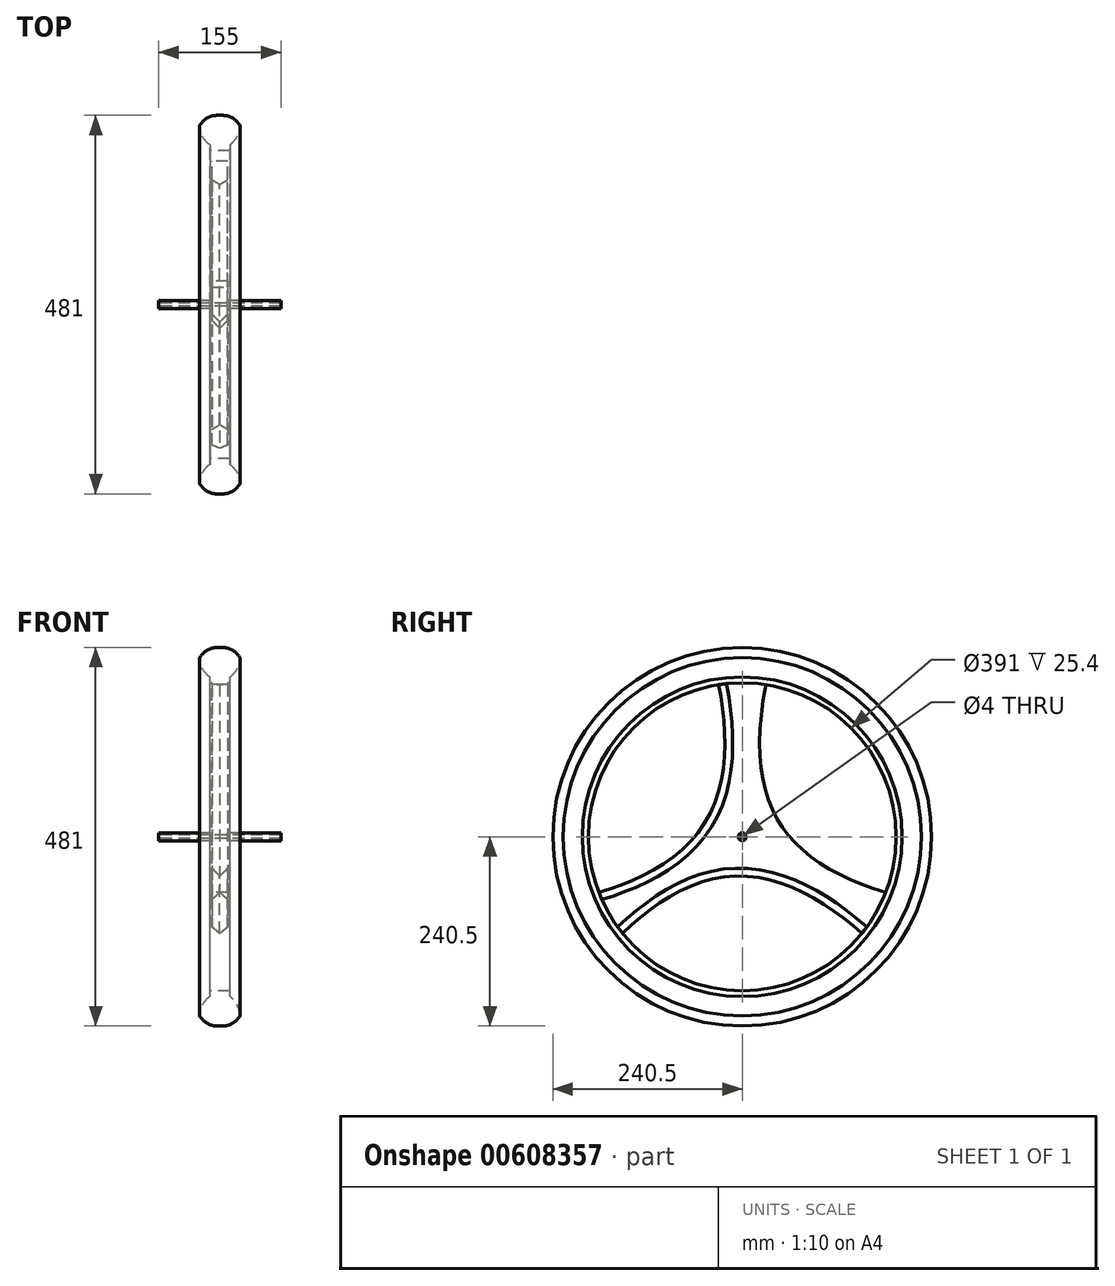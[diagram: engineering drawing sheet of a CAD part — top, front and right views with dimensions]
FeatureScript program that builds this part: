
annotation { "Feature Type Name" : "Feature", "Feature Type Description" : "" }
export const myFeature = defineFeature(function(context is Context, id is Id, definition is map)
    precondition{}
    {
        {
            var Q0;
            Q0=qCreatedBy(makeId("Right.planeOp"),FACE);
            var sketch = newSketch(context, id + "F0", { "sketchPlane" : qUnion([Q0])});
            skCircle(sketch, "E0", {"center": v(0, 0) * mm, "radius": 195.5 * mm});
            skCircle(sketch, "E1.0", {"center": v(0, 0) * mm, "radius": 240.5 * mm});
            skCircle(sketch, "E2", {"center": v(0, 0) * mm, "radius": 5 * mm});
            skCircle(sketch, "E3", {"center": v(0, 0) * mm, "radius": 2 * mm});
            skLineSegment(sketch, "E4", {"start": v(0, 0) * mm, "end": v(0, 195.5) * mm, "construction": true});
            skLineSegment(sketch, "E5", {"start": v(0, 0) * mm, "end": v(-169.3, -97.75) * mm, "construction": true});
            skLineSegment(sketch, "E6", {"start": v(0, 0) * mm, "end": v(169.3, -97.75) * mm, "construction": true});
            skFitSpline(sketch, "E7", {"points": [v(30, 193.18) * mm, v(182.3, -70.61) * mm], "startDerivative": vector(-90, -465.62) * mm, "endDerivative": vector(378.03, -114.33) * mm});
            skFitSpline(sketch, "E8.MirrorCS", {"points": [v(-30, 193.18) * mm, v(-182.3, -70.61) * mm], "startDerivative": vector(90, -465.62) * mm, "endDerivative": vector(-378.03, -114.33) * mm});
            skFitSpline(sketch, "E9.MirrorCS", {"points": [v(30, 193.18) * mm, v(182.3, -70.61) * mm], "startDerivative": vector(-90, -465.62) * mm, "endDerivative": vector(378.03, -114.33) * mm});
            skFitSpline(sketch, "E10.MirrorCS", {"points": [v(152.3, -122.57) * mm, v(-152.3, -122.57) * mm], "startDerivative": vector(-358.24, 310.75) * mm, "endDerivative": vector(-288.03, -270.22) * mm});
            skCircle(sketch, "E11", {"center": v(0, 0) * mm, "radius": 203 * mm});
            skSolve(sketch);
        }
        {
            var Q0;
            Q0=makeQuery(id+"F0.imprint","IMPRINT",FACE,{"disambiguationData":[TD([[makeQuery(id+"F0.imprint","IMPRINT",EDGE,{"derivedFrom":sQuery(id+"F0.wireOp",EDGE,"E11")}),1.0]])]});
            extrude(context, id + "F1", {"entities" : qUnion([Q0]), "endBound" : BoundingType.SYMMETRIC, "depth" : 25.4 * mm, "offsetDistance" : 25 * mm});
        }
        {
            var Q0;
            Q0=makeQuery(id+"F0.imprint","IMPRINT",FACE,{"disambiguationData":[TD([[makeQuery(id+"F0.imprint","IMPRINT",EDGE,{"derivedFrom":sQuery(id+"F0.wireOp",EDGE,"E2")}),-1.0]])]});
            extrude(context, id + "F2", {"entities" : qUnion([Q0]), "operationType" : NewBodyOperationType.ADD, "endBound" : BoundingType.SYMMETRIC, "depth" : 20 * mm, "offsetDistance" : 25 * mm});
        }
        {
            var Q0;
            Q0=makeQuery(id+"F0.imprint","IMPRINT",FACE,{"disambiguationData":[TD([[makeQuery(id+"F0.imprint","IMPRINT",EDGE,{"derivedFrom":sQuery(id+"F0.wireOp",EDGE,"E2")}),1.0]])]});
            extrude(context, id + "F3", {"entities" : qUnion([Q0]), "operationType" : NewBodyOperationType.ADD, "endBound" : BoundingType.SYMMETRIC, "depth" : 155 * mm, "offsetDistance" : 25 * mm});
        }
        {
            var Q0;
            Q0=makeQuery(id+"F0.imprint","IMPRINT",FACE,{"disambiguationData":[TD([[makeQuery(id+"F0.imprint","IMPRINT",EDGE,{"derivedFrom":sQuery(id+"F0.wireOp",EDGE,"E1.0")}),1.0]])]});
            extrude(context, id + "F4", {"entities" : qUnion([Q0]), "operationType" : NewBodyOperationType.ADD, "endBound" : BoundingType.SYMMETRIC, "depth" : 50.8 * mm, "offsetDistance" : 25 * mm});
        }
        {
            var Q0;
            Q0=makeQuery(id+"F4.opExtrude","CAP_EDGE",EDGE,{"disambiguationData":[OSD([sQuery(id+"F0.wireOp",EDGE,"E11")])],"isStart":true});
            var Q1;
            Q1=makeQuery(id+"F4.opExtrude","CAP_EDGE",EDGE,{"disambiguationData":[OSD([sQuery(id+"F0.wireOp",EDGE,"E11")])],"isStart":false});
            fillet(context, id + "F5", {"entities" : qUnion([Q0, Q1]), "radius" : 30 * mm, "tangentPropagation" : true, "allowEdgeOverflow" : false});
        }
        {
            var Q0;
            Q0=makeQuery(id+"F4.opExtrude","CAP_EDGE",EDGE,{"disambiguationData":[OSD([sQuery(id+"F0.wireOp",EDGE,"E1.0")])],"isStart":false});
            var Q1;
            Q1=makeQuery(id+"F4.opExtrude","CAP_EDGE",EDGE,{"disambiguationData":[OSD([sQuery(id+"F0.wireOp",EDGE,"E1.0")])],"isStart":true});
            fillet(context, id + "F6", {"entities" : qUnion([Q0, Q1]), "radius" : 25.4 * mm, "tangentPropagation" : true, "allowEdgeOverflow" : false});
        }
        {
            var Q0;
            Q0=makeQuery(id+"F2.opExtrude","CAP_EDGE",EDGE,{"disambiguationData":[OSD([sQuery(id+"F0.wireOp",EDGE,"E8.MirrorCS")])],"isStart":false});
            var Q1;
            Q1=makeQuery(id+"F2.opExtrude","CAP_EDGE",EDGE,{"disambiguationData":[OSD([sQuery(id+"F0.wireOp",EDGE,"E8.MirrorCS")])],"isStart":true});
            var Q2;
            Q2=makeQuery(id+"F2.opExtrude","CAP_EDGE",EDGE,{"disambiguationData":[OSD([sQuery(id+"F0.wireOp",EDGE,"E10.MirrorCS")])],"isStart":false});
            var Q3;
            Q3=makeQuery(id+"F2.opExtrude","CAP_EDGE",EDGE,{"disambiguationData":[OSD([sQuery(id+"F0.wireOp",EDGE,"E10.MirrorCS")])],"isStart":true});
            var Q4;
            Q4=makeQuery(id+"F2.opExtrude","CAP_EDGE",EDGE,{"disambiguationData":[OSD([sQuery(id+"F0.wireOp",EDGE,"E9.MirrorCS")])],"isStart":false});
            var Q5;
            Q5=makeQuery(id+"F2.opExtrude","CAP_EDGE",EDGE,{"disambiguationData":[OSD([sQuery(id+"F0.wireOp",EDGE,"E9.MirrorCS")])],"isStart":true});
            chamfer(context, id + "F7", {"entities" : qUnion([Q0, Q1, Q2, Q3, Q4, Q5]), "width" : 10 * mm, "tangentPropagation" : true});
        }
    });
